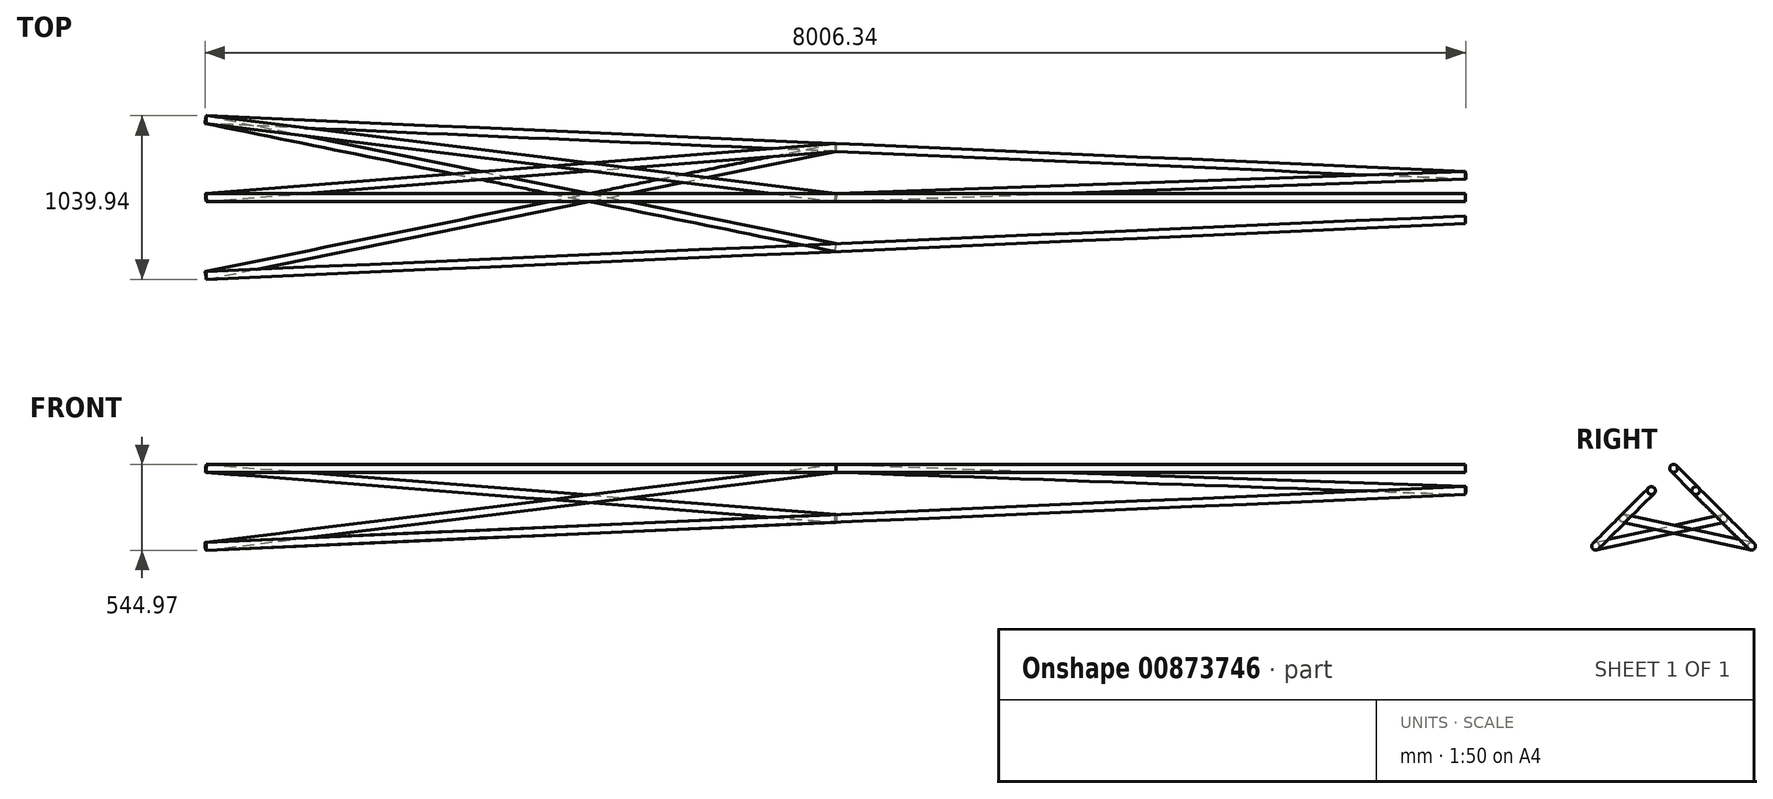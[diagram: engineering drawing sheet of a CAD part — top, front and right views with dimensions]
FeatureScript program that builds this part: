
annotation { "Feature Type Name" : "Feature", "Feature Type Description" : "" }
export const myFeature = defineFeature(function(context is Context, id is Id, definition is map)
    precondition{}
    {
        {
            var Q0;
            Q0=qCreatedBy(makeId("Right.planeOp"),FACE);
            var sketch = newSketch(context, id + "F0", { "sketchPlane" : qUnion([Q0])});
            skCircle(sketch, "E0", {"center": v(0, 0) * mm, "radius": 25 * mm});
            skCircle(sketch, "E1", {"center": v(-494.97, -494.97) * mm, "radius": 25 * mm});
            skCircle(sketch, "E2", {"center": v(494.97, -494.97) * mm, "radius": 25 * mm});
            skLineSegment(sketch, "E3", {"start": v(0, 0) * mm, "end": v(-494.97, -494.97) * mm});
            skLineSegment(sketch, "E4", {"start": v(494.97, -494.97) * mm, "end": v(-494.97, -494.97) * mm});
            skLineSegment(sketch, "E5", {"start": v(0, 0) * mm, "end": v(494.97, -494.97) * mm});
            skSolve(sketch);
        }
        {
            var Q0;
            {var subQ0=sQuery(id+"F0.wireOp",EDGE,"E3");var subQ1=sQuery(id+"F0.wireOp",EDGE,"E0");var subQ2=makeQuery(id+"F0.imprint","INTERSECT",VERTEX,{"derivedFrom":[subQ1,subQ0]});Q0=makeQuery(id+"F0.imprint","IMPRINT",FACE,{"disambiguationData":[TD([[makeQuery(id+"F0.imprint","IMPRINT",EDGE,{"disambiguationData":[TD([[subQ2,1.0]])],"derivedFrom":subQ1}),1.0]])]});}
            var Q1;
            {var subQ0=sQuery(id+"F0.wireOp",EDGE,"E3");var subQ1=sQuery(id+"F0.wireOp",EDGE,"E0");var subQ2=makeQuery(id+"F0.imprint","INTERSECT",VERTEX,{"derivedFrom":[subQ1,subQ0]});Q1=makeQuery(id+"F0.imprint","IMPRINT",FACE,{"disambiguationData":[TD([[makeQuery(id+"F0.imprint","IMPRINT",EDGE,{"disambiguationData":[TD([[subQ2,-1.0]])],"derivedFrom":subQ1}),1.0]])]});}
            extrude(context, id + "F1", {"entities" : qUnion([Q0, Q1]), "depth" : 8000 * mm, "offsetDistance" : 25 * mm});
        }
        {
            var Q0;
            Q0=makeQuery(id+"F1.opExtrude","CAP_FACE",FACE,{"disambiguationData":[OSD([sQuery(id+"F0.wireOp",EDGE,"E0")])],"isStart":false});
            cPlane(context, id + "F2", {"entities" : qUnion([Q0]), "cplaneType" : CPlaneType.OFFSET, "offset" : 0 * mm, "width" : 150 * mm, "height" : 150 * mm});
        }
        {
            var Q0;
            Q0=qCreatedBy(id+"F2.planeOp",FACE);
            var sketch = newSketch(context, id + "F3", { "sketchPlane" : qUnion([Q0])});
            skCircle(sketch, "E6", {"center": v(-141.42, -141.42) * mm, "radius": 25 * mm});
            skCircle(sketch, "E7", {"center": v(141.42, -141.42) * mm, "radius": 25 * mm});
            skLineSegment(sketch, "E8", {"start": v(0, 0) * mm, "end": v(-141.42, -141.42) * mm});
            skLineSegment(sketch, "E9", {"start": v(-141.42, -141.42) * mm, "end": v(141.42, -141.42) * mm});
            skLineSegment(sketch, "E10", {"start": v(141.42, -141.42) * mm, "end": v(0, 0) * mm});
            skSolve(sketch);
        }
        {
            var Q0;
            Q0=sQuery(id+"F3.wireOp",VERTEX,"E8.end");
            var Q1;
            Q1=sQuery(id+"F0.wireOp",VERTEX,"E4.start");
            var Q2;
            Q2=sQuery(id+"F0.wireOp",VERTEX,"E3.end");
            cPlane(context, id + "F4", {"entities" : qUnion([Q0, Q1, Q2]), "cplaneType" : CPlaneType.THREE_POINT, "offset" : 25 * mm, "width" : 150 * mm, "height" : 150 * mm});
        }
        {
            var Q0;
            Q0=qCreatedBy(id+"F4.planeOp",FACE);
            var sketch = newSketch(context, id + "F5", { "sketchPlane" : qUnion([Q0])});
            skLineSegment(sketch, "E11", {"start": v(-21.85, -494.97) * mm, "end": v(7985.96, -141.42) * mm});
            skLineSegment(sketch, "E12", {"start": v(7985.96, 141.42) * mm, "end": v(-21.85, 494.97) * mm});
            skSolve(sketch);
        }
        {
            var Q0;
            {var subQ0=sQuery(id+"F0.wireOp",EDGE,"E4");var subQ1=sQuery(id+"F0.wireOp",EDGE,"E2");var subQ2=makeQuery(id+"F0.imprint","INTERSECT",VERTEX,{"derivedFrom":[subQ1,subQ0]});Q0=makeQuery(id+"F0.imprint","IMPRINT",FACE,{"disambiguationData":[TD([[makeQuery(id+"F0.imprint","IMPRINT",EDGE,{"disambiguationData":[TD([[subQ2,-1.0]])],"derivedFrom":subQ1}),1.0]])]});}
            var Q1;
            {var subQ0=sQuery(id+"F0.wireOp",EDGE,"E4");var subQ1=sQuery(id+"F0.wireOp",EDGE,"E2");var subQ2=makeQuery(id+"F0.imprint","INTERSECT",VERTEX,{"derivedFrom":[subQ1,subQ0]});Q1=makeQuery(id+"F0.imprint","IMPRINT",FACE,{"disambiguationData":[TD([[makeQuery(id+"F0.imprint","IMPRINT",EDGE,{"disambiguationData":[TD([[subQ2,1.0]])],"derivedFrom":subQ1}),1.0]])]});}
            var Q2;
            Q2=sQuery(id+"F5.wireOp",EDGE,"E11");
            sweep(context, id + "F6", {"profiles" : qUnion([Q0, Q1]), "path" : qUnion([Q2])});
        }
        {
            var Q0;
            {var subQ0=sQuery(id+"F0.wireOp",EDGE,"E3");var subQ1=sQuery(id+"F0.wireOp",EDGE,"E1");var subQ2=makeQuery(id+"F0.imprint","INTERSECT",VERTEX,{"derivedFrom":[subQ1,subQ0]});Q0=makeQuery(id+"F0.imprint","IMPRINT",FACE,{"disambiguationData":[TD([[makeQuery(id+"F0.imprint","IMPRINT",EDGE,{"disambiguationData":[TD([[subQ2,-1.0]])],"derivedFrom":subQ1}),1.0]])]});}
            var Q1;
            {var subQ0=sQuery(id+"F0.wireOp",EDGE,"E3");var subQ1=sQuery(id+"F0.wireOp",EDGE,"E1");var subQ2=makeQuery(id+"F0.imprint","INTERSECT",VERTEX,{"derivedFrom":[subQ1,subQ0]});Q1=makeQuery(id+"F0.imprint","IMPRINT",FACE,{"disambiguationData":[TD([[makeQuery(id+"F0.imprint","IMPRINT",EDGE,{"disambiguationData":[TD([[subQ2,1.0]])],"derivedFrom":subQ1}),1.0]])]});}
            var Q2;
            Q2=sQuery(id+"F5.wireOp",EDGE,"E12");
            sweep(context, id + "F7", {"profiles" : qUnion([Q0, Q1]), "path" : qUnion([Q2])});
        }
        {
            var Q0;
            Q0=sQuery(id+"F0.wireOp",VERTEX,"E3.start");
            var Q1;
            Q1=sQuery(id+"F0.wireOp",VERTEX,"E3.end");
            var Q2;
            Q2=sQuery(id+"F3.wireOp",VERTEX,"E8.start");
            cPlane(context, id + "F8", {"entities" : qUnion([Q0, Q1, Q2]), "cplaneType" : CPlaneType.THREE_POINT, "offset" : 25 * mm, "width" : 150 * mm, "height" : 150 * mm});
        }
        {
            var Q0;
            Q0=qCreatedBy(id+"F8.planeOp",FACE);
            var sketch = newSketch(context, id + "F9", { "sketchPlane" : qUnion([Q0])});
            skCircle(sketch, "E13", {"center": v(25, 0) * mm, "radius": 25 * mm});
            skCircle(sketch, "E14", {"center": v(7975, 0) * mm, "radius": 25 * mm});
            skSolve(sketch);
        }
        {
            var Q0;
            Q0=sQuery(id+"F0.wireOp",VERTEX,"E4.start");
            var Q1;
            Q1=sQuery(id+"F0.wireOp",VERTEX,"E3.start");
            var Q2;
            Q2=sQuery(id+"F3.wireOp",VERTEX,"E9.end");
            cPlane(context, id + "F10", {"entities" : qUnion([Q0, Q1, Q2]), "cplaneType" : CPlaneType.THREE_POINT, "offset" : 0 * mm, "width" : 150 * mm, "height" : 150 * mm});
        }
        {
            var Q0;
            Q0=qCreatedBy(id+"F10.planeOp",FACE);
            var sketch = newSketch(context, id + "F11", { "sketchPlane" : qUnion([Q0])});
            skLineSegment(sketch, "E15", {"start": v(0, 0) * mm, "end": v(0, -700) * mm});
            skLineSegment(sketch, "E16", {"start": v(8000, 0) * mm, "end": v(8000, -200) * mm});
            skSolve(sketch);
        }
        {
            var Q0;
            Q0=qCreatedBy(id+"F10.planeOp",FACE);
            var sketch = newSketch(context, id + "F12", { "sketchPlane" : qUnion([Q0])});
            skCircle(sketch, "E17", {"center": v(25, 0) * mm, "radius": 25 * mm});
            skCircle(sketch, "E18", {"center": v(7975, 0) * mm, "radius": 25 * mm});
            skSolve(sketch);
        }
        {
            var Q0;
            Q0=sQuery(id+"F0.wireOp",VERTEX,"E4.start");
            var Q1;
            Q1=sQuery(id+"F0.wireOp",EDGE,"E4");
            cPlane(context, id + "F13", {"entities" : qUnion([Q0, Q1]), "cplaneType" : CPlaneType.LINE_POINT, "offset" : 25 * mm, "width" : 150 * mm, "height" : 150 * mm});
        }
        {
            var Q0;
            Q0=qCreatedBy(id+"F13.planeOp",FACE);
            var sketch = newSketch(context, id + "F14", { "sketchPlane" : qUnion([Q0])});
            skCircle(sketch, "E19", {"center": v(25, -494.97) * mm, "radius": 25 * mm});
            skSolve(sketch);
        }
        {
            var Q0;
            Q0=sQuery(id+"F3.wireOp",VERTEX,"E9.end");
            var Q1;
            Q1=sQuery(id+"F3.wireOp",EDGE,"E9");
            cPlane(context, id + "F15", {"entities" : qUnion([Q0, Q1]), "cplaneType" : CPlaneType.LINE_POINT, "offset" : 25 * mm, "width" : 150 * mm, "height" : 150 * mm});
        }
        {
            var Q0;
            Q0=qCreatedBy(id+"F15.planeOp",FACE);
            var sketch = newSketch(context, id + "F16", { "sketchPlane" : qUnion([Q0])});
            skCircle(sketch, "E20", {"center": v(-7975, -142.53) * mm, "radius": 25 * mm});
            skSolve(sketch);
        }
        {
            var Q0;
            Q0=qCreatedBy(makeId("Right.planeOp"),FACE);
            cPlane(context, id + "F17", {"entities" : qUnion([Q0]), "cplaneType" : CPlaneType.OFFSET, "offset" : 4000 * mm, "width" : 150 * mm, "height" : 150 * mm});
        }
        {
            var Q0;
            Q0=qCreatedBy(id+"F17.planeOp",FACE);
            var sketch = newSketch(context, id + "F18", { "sketchPlane" : qUnion([Q0])});
            skLineSegment(sketch, "E21", {"start": v(0, 0) * mm, "end": v(318.2, -318.2) * mm});
            skLineSegment(sketch, "E22", {"start": v(318.2, -318.2) * mm, "end": v(-318.2, -318.2) * mm});
            skLineSegment(sketch, "E23", {"start": v(-318.2, -318.2) * mm, "end": v(0, 0) * mm});
            skSolve(sketch);
        }
        {
            var Q0;
            Q0=sQuery(id+"F18.wireOp",VERTEX,"E21.start");
            var Q1;
            Q1=sQuery(id+"F18.wireOp",EDGE,"E23");
            cPlane(context, id + "F19", {"entities" : qUnion([Q0, Q1]), "cplaneType" : CPlaneType.LINE_POINT, "offset" : 25 * mm, "width" : 150 * mm, "height" : 150 * mm});
        }
        {
            var Q0;
            Q0=qCreatedBy(id+"F19.planeOp",FACE);
            var sketch = newSketch(context, id + "F20", { "sketchPlane" : qUnion([Q0])});
            skCircle(sketch, "E24", {"center": v(4000, 0) * mm, "radius": 25 * mm});
            skSolve(sketch);
        }
        {
            var Q0;
            Q0=sQuery(id+"F18.wireOp",EDGE,"E21");
            var Q1;
            Q1=sQuery(id+"F18.wireOp",VERTEX,"E21.start");
            cPlane(context, id + "F21", {"entities" : qUnion([Q0, Q1]), "cplaneType" : CPlaneType.LINE_POINT, "offset" : 25 * mm, "width" : 150 * mm, "height" : 150 * mm});
        }
        {
            var Q0;
            Q0=qCreatedBy(id+"F21.planeOp",FACE);
            var sketch = newSketch(context, id + "F22", { "sketchPlane" : qUnion([Q0])});
            skCircle(sketch, "E25", {"center": v(4000, 0) * mm, "radius": 25 * mm});
            skSolve(sketch);
        }
        {
            var Q0;
            Q0=sQuery(id+"F18.wireOp",VERTEX,"E21.end");
            var Q1;
            Q1=sQuery(id+"F18.wireOp",EDGE,"E22");
            cPlane(context, id + "F23", {"entities" : qUnion([Q0, Q1]), "cplaneType" : CPlaneType.LINE_POINT, "offset" : 25 * mm, "width" : 150 * mm, "height" : 150 * mm});
        }
        {
            var Q0;
            Q0=qCreatedBy(id+"F23.planeOp",FACE);
            var sketch = newSketch(context, id + "F24", { "sketchPlane" : qUnion([Q0])});
            skCircle(sketch, "E26", {"center": v(4000, -318.2) * mm, "radius": 25 * mm});
            skSolve(sketch);
        }
        {
            var Q0;
            Q0=qCreatedBy(id+"F8.planeOp",FACE);
            var sketch = newSketch(context, id + "F25", { "sketchPlane" : qUnion([Q0])});
            skLineSegment(sketch, "E27", {"start": v(0, 0) * mm, "end": v(4000, 450) * mm});
            skLineSegment(sketch, "E28", {"start": v(0, 700) * mm, "end": v(4000, 0) * mm});
            skLineSegment(sketch, "E29", {"start": v(4000, 0) * mm, "end": v(8000, 200) * mm});
            skLineSegment(sketch, "E30", {"start": v(8000, 0) * mm, "end": v(4000, 450) * mm});
            skSolve(sketch);
        }
        {
            var Q0;
            Q0=sQuery(id+"F25.wireOp",EDGE,"E27");
            var Q1;
            Q1=sQuery(id+"F0.wireOp",VERTEX,"E3.start");
            cPlane(context, id + "F26", {"entities" : qUnion([Q0, Q1]), "cplaneType" : CPlaneType.LINE_POINT, "offset" : 25 * mm, "width" : 150 * mm, "height" : 150 * mm});
        }
        {
            var Q0;
            Q0=qCreatedBy(id+"F26.planeOp",FACE);
            var sketch = newSketch(context, id + "F27", { "sketchPlane" : qUnion([Q0])});
            skCircle(sketch, "E31", {"center": v(0, 0) * mm, "radius": 25 * mm});
            skSolve(sketch);
        }
        {
            var Q0;
            Q0=sQuery(id+"F0.wireOp",VERTEX,"E3.end");
            var Q1;
            Q1=sQuery(id+"F25.wireOp",EDGE,"E28");
            cPlane(context, id + "F28", {"entities" : qUnion([Q0, Q1]), "cplaneType" : CPlaneType.LINE_POINT, "offset" : 25 * mm, "width" : 150 * mm, "height" : 150 * mm});
        }
        {
            var Q0;
            Q0=qCreatedBy(id+"F28.planeOp",FACE);
            var sketch = newSketch(context, id + "F29", { "sketchPlane" : qUnion([Q0])});
            skCircle(sketch, "E32", {"center": v(-483.87, -491.23) * mm, "radius": 25 * mm});
            skSolve(sketch);
        }
        {
            var Q0;
            Q0=sQuery(id+"F18.wireOp",VERTEX,"E21.start");
            var Q1;
            Q1=sQuery(id+"F25.wireOp",EDGE,"E29");
            cPlane(context, id + "F30", {"entities" : qUnion([Q0, Q1]), "cplaneType" : CPlaneType.LINE_POINT, "offset" : 25 * mm, "width" : 150 * mm, "height" : 150 * mm});
        }
        {
            var Q0;
            Q0=qCreatedBy(id+"F30.planeOp",FACE);
            var sketch = newSketch(context, id + "F31", { "sketchPlane" : qUnion([Q0])});
            skCircle(sketch, "E33", {"center": v(141.16, 141.33) * mm, "radius": 25 * mm});
            skSolve(sketch);
        }
        {
            var Q0;
            Q0=sQuery(id+"F18.wireOp",VERTEX,"E22.end");
            var Q1;
            Q1=sQuery(id+"F25.wireOp",EDGE,"E30");
            cPlane(context, id + "F32", {"entities" : qUnion([Q0, Q1]), "cplaneType" : CPlaneType.LINE_POINT, "offset" : 25 * mm, "width" : 150 * mm, "height" : 150 * mm});
        }
        {
            var Q0;
            Q0=qCreatedBy(id+"F32.planeOp",FACE);
            var sketch = newSketch(context, id + "F33", { "sketchPlane" : qUnion([Q0])});
            skCircle(sketch, "E34", {"center": v(630.42, -634.4) * mm, "radius": 25 * mm});
            skSolve(sketch);
        }
        {
            var Q0;
            Q0=qCreatedBy(id+"F10.planeOp",FACE);
            var sketch = newSketch(context, id + "F34", { "sketchPlane" : qUnion([Q0])});
            skLineSegment(sketch, "E35", {"start": v(0, 0) * mm, "end": v(4000, -450) * mm});
            skLineSegment(sketch, "E36", {"start": v(4000, 0) * mm, "end": v(0, -700) * mm});
            skLineSegment(sketch, "E37", {"start": v(4000, 0) * mm, "end": v(8000, -200) * mm});
            skLineSegment(sketch, "E38", {"start": v(8000, 0) * mm, "end": v(4000, -450) * mm});
            skSolve(sketch);
        }
        {
            var Q0;
            Q0=qCreatedBy(id+"F4.planeOp",FACE);
            var sketch = newSketch(context, id + "F35", { "sketchPlane" : qUnion([Q0])});
            skLineSegment(sketch, "E39", {"start": v(-21.85, 494.97) * mm, "end": v(3982.05, -318.2) * mm});
            skLineSegment(sketch, "E40", {"start": v(3982.05, 318.2) * mm, "end": v(-21.85, -494.97) * mm});
            skLineSegment(sketch, "E41", {"start": v(3982.05, 318.2) * mm, "end": v(7985.96, -141.42) * mm});
            skLineSegment(sketch, "E42", {"start": v(7985.96, 141.42) * mm, "end": v(3982.05, -318.2) * mm});
            skSolve(sketch);
        }
        {
            var Q0;
            Q0=sQuery(id+"F35.wireOp",EDGE,"E40");
            var Q1;
            Q1=sQuery(id+"F0.wireOp",VERTEX,"E4.start");
            cPlane(context, id + "F36", {"entities" : qUnion([Q0, Q1]), "cplaneType" : CPlaneType.LINE_POINT, "offset" : 25 * mm, "width" : 150 * mm, "height" : 150 * mm});
        }
        {
            var Q0;
            Q0=qCreatedBy(id+"F36.planeOp",FACE);
            var sketch = newSketch(context, id + "F37", { "sketchPlane" : qUnion([Q0])});
            skCircle(sketch, "E43", {"center": v(-480.72, -494.5) * mm, "radius": 25 * mm});
            skSolve(sketch);
        }
        {
            var Q0;
            Q0 = qSketchRegion(id + "F37", true);
            var Q1;
            Q1=sQuery(id+"F35.wireOp",EDGE,"E40");
            sweep(context, id + "F38", {"profiles" : qUnion([Q0]), "path" : qUnion([Q1])});
        }
        {
            var Q0;
            Q0=sQuery(id+"F34.wireOp",EDGE,"E35");
            var Q1;
            Q1=sQuery(id+"F0.wireOp",VERTEX,"E3.start");
            cPlane(context, id + "F39", {"entities" : qUnion([Q0, Q1]), "cplaneType" : CPlaneType.LINE_POINT, "offset" : 25 * mm, "width" : 150 * mm, "height" : 150 * mm});
        }
        {
            var Q0;
            Q0=qCreatedBy(id+"F39.planeOp",FACE);
            var sketch = newSketch(context, id + "F40", { "sketchPlane" : qUnion([Q0])});
            skCircle(sketch, "E44", {"center": v(0, 0) * mm, "radius": 25 * mm});
            skSolve(sketch);
        }
        {
            var Q0;
            Q0 = qSketchRegion(id + "F40", true);
            var Q1;
            Q1=sQuery(id+"F34.wireOp",EDGE,"E35");
            sweep(context, id + "F41", {"profiles" : qUnion([Q0]), "path" : qUnion([Q1])});
        }
        {
            var Q0;
            Q0=sQuery(id+"F35.wireOp",EDGE,"E39");
            var Q1;
            Q1=sQuery(id+"F0.wireOp",VERTEX,"E3.end");
            cPlane(context, id + "F42", {"entities" : qUnion([Q0, Q1]), "cplaneType" : CPlaneType.LINE_POINT, "offset" : 25 * mm, "width" : 150 * mm, "height" : 150 * mm});
        }
        {
            var Q0;
            Q0=qCreatedBy(id+"F42.planeOp",FACE);
            var sketch = newSketch(context, id + "F43", { "sketchPlane" : qUnion([Q0])});
            skCircle(sketch, "E45", {"center": v(-480.72, -494.5) * mm, "radius": 25 * mm});
            skSolve(sketch);
        }
        {
            var Q0;
            Q0 = qSketchRegion(id + "F43", true);
            var Q1;
            Q1=sQuery(id+"F35.wireOp",EDGE,"E39");
            sweep(context, id + "F44", {"profiles" : qUnion([Q0]), "path" : qUnion([Q1])});
        }
        {
            var Q0;
            Q0=sQuery(id+"F34.wireOp",EDGE,"E36");
            var Q1;
            Q1=sQuery(id+"F0.wireOp",VERTEX,"E4.start");
            cPlane(context, id + "F45", {"entities" : qUnion([Q0, Q1]), "cplaneType" : CPlaneType.LINE_POINT, "offset" : 25 * mm, "width" : 150 * mm, "height" : 150 * mm});
        }
        {
            var Q0;
            Q0=qCreatedBy(id+"F45.planeOp",FACE);
            var sketch = newSketch(context, id + "F46", { "sketchPlane" : qUnion([Q0])});
            skCircle(sketch, "E46", {"center": v(-483.87, -491.23) * mm, "radius": 25 * mm});
            skSolve(sketch);
        }
        {
            var Q0;
            Q0 = qSketchRegion(id + "F46", true);
            var Q1;
            Q1=sQuery(id+"F34.wireOp",EDGE,"E36");
            sweep(context, id + "F47", {"profiles" : qUnion([Q0]), "path" : qUnion([Q1])});
        }
        {
            var Q0;
            Q0=sQuery(id+"F34.wireOp",EDGE,"E37");
            var Q1;
            Q1=sQuery(id+"F18.wireOp",VERTEX,"E21.start");
            cPlane(context, id + "F48", {"entities" : qUnion([Q0, Q1]), "cplaneType" : CPlaneType.LINE_POINT, "offset" : 25 * mm, "width" : 150 * mm, "height" : 150 * mm});
        }
        {
            var Q0;
            Q0=qCreatedBy(id+"F48.planeOp",FACE);
            var sketch = newSketch(context, id + "F49", { "sketchPlane" : qUnion([Q0])});
            skCircle(sketch, "E47", {"center": v(-141.16, 141.33) * mm, "radius": 25 * mm});
            skSolve(sketch);
        }
        {
            var Q0;
            Q0 = qSketchRegion(id + "F49", true);
            var Q1;
            Q1=sQuery(id+"F34.wireOp",EDGE,"E37");
            sweep(context, id + "F50", {"profiles" : qUnion([Q0]), "path" : qUnion([Q1])});
        }
    });
